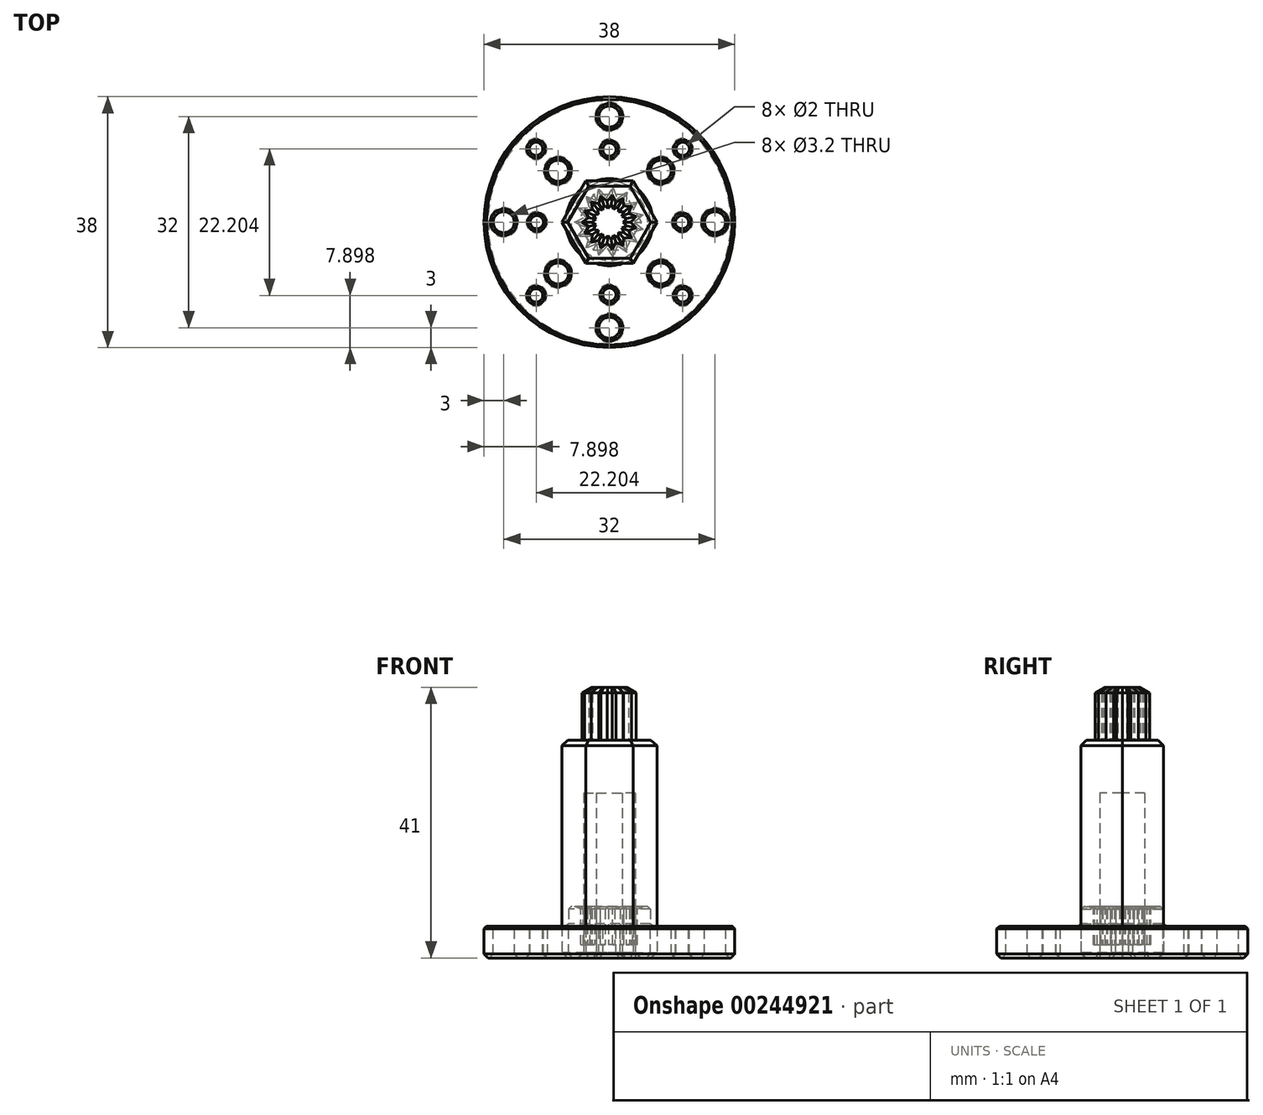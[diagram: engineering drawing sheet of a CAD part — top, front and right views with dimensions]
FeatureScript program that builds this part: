
annotation { "Feature Type Name" : "Feature", "Feature Type Description" : "" }
export const myFeature = defineFeature(function(context is Context, id is Id, definition is map)
    precondition{}
    {
        {
            var Q0;
            Q0=qCreatedBy(makeId("Top.planeOp"),FACE);
            var sketch = newSketch(context, id + "F0", { "sketchPlane" : qUnion([Q0])});
            skCircle(sketch, "E0", {"center": v(0, 0) * mm, "radius": 19 * mm});
            skSolve(sketch);
        }
        {
            var Q0;
            Q0=qSketchRegion(id+"F0",true);
            extrude(context, id + "F1", {"entities" : qUnion([Q0]), "depth" : 4.8 * mm, "offsetDistance" : 25 * mm});
        }
        {
            var Q0;
            Q0=makeQuery(id+"F1.opExtrude","CAP_FACE",FACE,{"disambiguationData":[OSD([sQuery(id+"F0.wireOp",EDGE,"ZvkXPhkh-jxfF-Gfea-dxrh-XISQfD8u4X7v"),sQuery(id+"F0.wireOp",EDGE,"E0")])],"isStart":false});
            var sketch = newSketch(context, id + "F2", { "sketchPlane" : qUnion([Q0])});
            skCircle(sketch, "E1", {"center": v(11, 0) * mm, "radius": 1 * mm});
            skCircle(sketch, "E2.1.0", {"center": v(0, 11) * mm, "radius": 1 * mm});
            skCircle(sketch, "E2.2.0", {"center": v(-11, 0) * mm, "radius": 1 * mm});
            skCircle(sketch, "E2.3.0", {"center": v(0, -11) * mm, "radius": 1 * mm});
            skPoint(sketch, "E2.center", {"position": v(0, 0) * mm});
            skCircle(sketch, "E3", {"center": v(16, 0) * mm, "radius": 1.6 * mm});
            skCircle(sketch, "E4.1.0", {"center": v(0, 16) * mm, "radius": 1.6 * mm});
            skCircle(sketch, "E4.2.0", {"center": v(-16, 0) * mm, "radius": 1.6 * mm});
            skCircle(sketch, "E4.3.0", {"center": v(0, -16) * mm, "radius": 1.6 * mm});
            skLineSegment(sketch, "E5", {"start": v(0, 0) * mm, "end": v(7.78, 7.78) * mm});
            skLineSegment(sketch, "E6", {"start": v(7.78, 7.78) * mm, "end": v(11.1, 11.1) * mm});
            skCircle(sketch, "E7", {"center": v(7.78, 7.78) * mm, "radius": 1.6 * mm});
            skCircle(sketch, "E8", {"center": v(11.1, 11.1) * mm, "radius": 1 * mm});
            skCircle(sketch, "E9.1.0", {"center": v(-7.78, 7.78) * mm, "radius": 1.6 * mm});
            skCircle(sketch, "E9.1.1", {"center": v(-11.1, 11.1) * mm, "radius": 1 * mm});
            skCircle(sketch, "E9.2.0", {"center": v(-7.78, -7.78) * mm, "radius": 1.6 * mm});
            skCircle(sketch, "E9.2.1", {"center": v(-11.1, -11.1) * mm, "radius": 1 * mm});
            skCircle(sketch, "E9.3.0", {"center": v(7.78, -7.78) * mm, "radius": 1.6 * mm});
            skCircle(sketch, "E9.3.1", {"center": v(11.1, -11.1) * mm, "radius": 1 * mm});
            skSolve(sketch);
        }
        {
            var Q0;
            Q0=qSketchRegion(id+"F2",true);
            extrude(context, id + "F3", {"entities" : qUnion([Q0]), "operationType" : NewBodyOperationType.REMOVE, "oppositeDirection" : true, "depth" : 10 * mm, "offsetDistance" : 25 * mm});
        }
        {
            var Q0;
            Q0=makeQuery(id+"F1.opExtrude","CAP_FACE",FACE,{"disambiguationData":[OSD([sQuery(id+"F0.wireOp",EDGE,"E0")])],"isStart":false});
            var sketch = newSketch(context, id + "F4", { "sketchPlane" : qUnion([Q0])});
            skCircle(sketch, "E10", {"center": v(0, 0) * mm, "radius": 6.2 * mm});
            skSolve(sketch);
        }
        {
            var Q0;
            Q0=qSketchRegion(id+"F4",true);
            extrude(context, id + "F5", {"entities" : qUnion([Q0]), "operationType" : NewBodyOperationType.ADD, "depth" : 3 * mm, "offsetDistance" : 25 * mm});
        }
        {
            var Q0;
            Q0=makeQuery(id+"F5.opExtrude","CAP_FACE",FACE,{"disambiguationData":[OSD([sQuery(id+"F4.wireOp",EDGE,"E10")])],"isStart":false});
            var sketch = newSketch(context, id + "F6", { "sketchPlane" : qUnion([Q0])});
            skLineSegment(sketch, "E11", {"start": v(3.1, 0) * mm, "end": v(4.3, 0.94) * mm});
            skLineSegment(sketch, "E12.MirrorCS", {"start": v(3.1, 0) * mm, "end": v(4.3, -0.94) * mm});
            skLineSegment(sketch, "E13.1.0", {"start": v(2.83, 1.26) * mm, "end": v(3.55, 2.6) * mm});
            skLineSegment(sketch, "E13.1.1", {"start": v(2.83, 1.26) * mm, "end": v(4.3, 0.9) * mm});
            skLineSegment(sketch, "E13.2.0", {"start": v(2.07, 2.3) * mm, "end": v(2.18, 3.82) * mm});
            skLineSegment(sketch, "E13.2.1", {"start": v(2.07, 2.3) * mm, "end": v(3.57, 2.57) * mm});
            skLineSegment(sketch, "E13.3.0", {"start": v(0.96, 2.95) * mm, "end": v(0.44, 4.38) * mm});
            skLineSegment(sketch, "E13.3.1", {"start": v(0.96, 2.95) * mm, "end": v(2.22, 3.8) * mm});
            skLineSegment(sketch, "E13.4.0", {"start": v(-0.32, 3.08) * mm, "end": v(-1.38, 4.18) * mm});
            skLineSegment(sketch, "E13.4.1", {"start": v(-0.32, 3.08) * mm, "end": v(0.48, 4.37) * mm});
            skLineSegment(sketch, "E13.5.0", {"start": v(-1.55, 2.68) * mm, "end": v(-2.96, 3.26) * mm});
            skLineSegment(sketch, "E13.5.1", {"start": v(-1.55, 2.68) * mm, "end": v(-1.34, 4.2) * mm});
            skLineSegment(sketch, "E13.6.0", {"start": v(-2.5, 1.82) * mm, "end": v(-4.03, 1.77) * mm});
            skLineSegment(sketch, "E13.6.1", {"start": v(-2.5, 1.82) * mm, "end": v(-2.93, 3.29) * mm});
            skLineSegment(sketch, "E13.7.0", {"start": v(-3.03, 0.64) * mm, "end": v(-4.4, -0.02) * mm});
            skLineSegment(sketch, "E13.7.1", {"start": v(-3.03, 0.64) * mm, "end": v(-4.01, 1.81) * mm});
            skLineSegment(sketch, "E13.8.0", {"start": v(-3.03, -0.64) * mm, "end": v(-4.01, -1.81) * mm});
            skLineSegment(sketch, "E13.8.1", {"start": v(-3.03, -0.64) * mm, "end": v(-4.4, 0.02) * mm});
            skLineSegment(sketch, "E13.9.0", {"start": v(-2.5, -1.82) * mm, "end": v(-2.93, -3.29) * mm});
            skLineSegment(sketch, "E13.9.1", {"start": v(-2.5, -1.82) * mm, "end": v(-4.03, -1.77) * mm});
            skLineSegment(sketch, "E13.10.0", {"start": v(-1.55, -2.68) * mm, "end": v(-1.34, -4.2) * mm});
            skLineSegment(sketch, "E13.10.1", {"start": v(-1.55, -2.68) * mm, "end": v(-2.96, -3.26) * mm});
            skLineSegment(sketch, "E13.11.0", {"start": v(-0.32, -3.08) * mm, "end": v(0.48, -4.37) * mm});
            skLineSegment(sketch, "E13.11.1", {"start": v(-0.32, -3.08) * mm, "end": v(-1.38, -4.18) * mm});
            skLineSegment(sketch, "E13.12.0", {"start": v(0.96, -2.95) * mm, "end": v(2.22, -3.8) * mm});
            skLineSegment(sketch, "E13.12.1", {"start": v(0.96, -2.95) * mm, "end": v(0.44, -4.38) * mm});
            skLineSegment(sketch, "E13.13.0", {"start": v(2.07, -2.3) * mm, "end": v(3.57, -2.57) * mm});
            skLineSegment(sketch, "E13.13.1", {"start": v(2.07, -2.3) * mm, "end": v(2.18, -3.82) * mm});
            skLineSegment(sketch, "E13.14.0", {"start": v(2.83, -1.26) * mm, "end": v(4.3, -0.9) * mm});
            skLineSegment(sketch, "E13.14.1", {"start": v(2.83, -1.26) * mm, "end": v(3.55, -2.6) * mm});
            skPoint(sketch, "E13.center", {"position": v(0, 0) * mm});
            skSolve(sketch);
        }
        {
            var Q0;
            Q0=qSketchRegion(id+"F6",true);
            extrude(context, id + "F7", {"entities" : qUnion([Q0]), "operationType" : NewBodyOperationType.REMOVE, "oppositeDirection" : true, "depth" : 25 * mm, "offsetDistance" : 25 * mm});
        }
        {
            var Q0;
            Q0=qCreatedBy(makeId("Top.planeOp"),FACE);
            var sketch = newSketch(context, id + "F8", { "sketchPlane" : qUnion([Q0])});
            skCircle(sketch, "E14", {"center": v(0, 0) * mm, "radius": 6 * mm});
            skCircle(sketch, "E15", {"center": v(0, 0) * mm, "radius": 1.8 * mm});
            skSolve(sketch);
        }
        {
            var Q0;
            Q0 = qSketchRegion(id + "F8", true);
            extrude(context, id + "F9", {"entities" : qUnion([Q0]), "operationType" : NewBodyOperationType.ADD, "depth" : 2 * mm, "offsetDistance" : 25 * mm});
        }
        {
            var Q0;
            Q0=makeQuery(id+"F1.opExtrude","CAP_FACE",FACE,{"disambiguationData":[OSD([sQuery(id+"F0.wireOp",EDGE,"E0")])],"isStart":true});
            chamfer(context, id + "F10", {"entities" : qUnion([Q0]), "width" : .6 * mm, "tangentPropagation" : true});
        }
        {
            var Q0;
            Q0=makeQuery(id+"F5.opExtrude","CAP_FACE",FACE,{"disambiguationData":[OSD([sQuery(id+"F4.wireOp",EDGE,"E10")])],"isStart":false});
            var Q1;
            Q1=makeQuery(id+"F1.opExtrude","CAP_FACE",FACE,{"disambiguationData":[OSD([sQuery(id+"F0.wireOp",EDGE,"E0")])],"isStart":false});
            chamfer(context, id + "F11", {"entities" : qUnion([Q0, Q1]), "width" : .4 * mm, "tangentPropagation" : true});
        }
        {
            var Q0;
            Q0=qCreatedBy(makeId("Top.planeOp"),FACE);
            var sketch = newSketch(context, id + "F12", { "sketchPlane" : qUnion([Q0])});
            skCircle(sketch, "E16.cCircle", {"center": v(0, 0) * mm, "radius": 6.25 * mm, "construction": true});
            skLineSegment(sketch, "E16.0", {"start": v(-3.6, 6.25) * mm, "end": v(3.6, 6.25) * mm});
            skLineSegment(sketch, "E16.1", {"start": v(3.6, 6.25) * mm, "end": v(7.22, 0) * mm});
            skLineSegment(sketch, "E16.2", {"start": v(7.22, 0) * mm, "end": v(3.6, -6.25) * mm});
            skLineSegment(sketch, "E16.3", {"start": v(3.6, -6.25) * mm, "end": v(-3.6, -6.25) * mm});
            skLineSegment(sketch, "E16.4", {"start": v(-3.6, -6.25) * mm, "end": v(-7.22, 0) * mm});
            skLineSegment(sketch, "E16.5", {"start": v(-7.22, 0) * mm, "end": v(-3.6, 6.25) * mm});
            skPoint(sketch, "E16.0.midPoint", {"position": v(0, 6.25) * mm});
            skSolve(sketch);
        }
        {
            var Q0;
            Q0 = qSketchRegion(id + "F12", true);
            extrude(context, id + "F13", {"entities" : qUnion([Q0]), "depth" : 30 * mm, "offsetDistance" : 25 * mm});
        }
        {
            var Q0;
            Q0=makeQuery(id+"F13.opExtrude","CAP_FACE",FACE,{"disambiguationData":[OSD([sQuery(id+"F12.wireOp",EDGE,"E16.0"),sQuery(id+"F12.wireOp",EDGE,"E16.1"),sQuery(id+"F12.wireOp",EDGE,"E16.2"),sQuery(id+"F12.wireOp",EDGE,"E16.3"),sQuery(id+"F12.wireOp",EDGE,"E16.4"),sQuery(id+"F12.wireOp",EDGE,"E16.5")])],"isStart":true});
            var sketch = newSketch(context, id + "F14", { "sketchPlane" : qUnion([Q0])});
            skCircle(sketch, "E17.cCircle", {"center": v(0, 0) * mm, "radius": 3.4 * mm, "construction": true});
            skLineSegment(sketch, "E17.0", {"start": v(-1.96, 3.4) * mm, "end": v(1.96, 3.4) * mm});
            skLineSegment(sketch, "E17.1", {"start": v(1.96, 3.4) * mm, "end": v(3.93, 0) * mm});
            skLineSegment(sketch, "E17.2", {"start": v(3.93, 0) * mm, "end": v(1.96, -3.4) * mm});
            skLineSegment(sketch, "E17.3", {"start": v(1.96, -3.4) * mm, "end": v(-1.96, -3.4) * mm});
            skLineSegment(sketch, "E17.4", {"start": v(-1.96, -3.4) * mm, "end": v(-3.93, 0) * mm});
            skLineSegment(sketch, "E17.5", {"start": v(-3.93, 0) * mm, "end": v(-1.96, 3.4) * mm});
            skPoint(sketch, "E17.0.midPoint", {"position": v(0, 3.4) * mm});
            skSolve(sketch);
        }
        {
            var Q0;
            Q0 = qSketchRegion(id + "F14", true);
            extrude(context, id + "F15", {"entities" : qUnion([Q0]), "operationType" : NewBodyOperationType.REMOVE, "oppositeDirection" : true, "depth" : 25 * mm, "offsetDistance" : 25 * mm});
        }
        {
            var Q0;
            Q0=makeQuery(id+"F13.opExtrude","CAP_FACE",FACE,{"disambiguationData":[OSD([sQuery(id+"F12.wireOp",EDGE,"E16.0"),sQuery(id+"F12.wireOp",EDGE,"E16.1"),sQuery(id+"F12.wireOp",EDGE,"E16.2"),sQuery(id+"F12.wireOp",EDGE,"E16.3"),sQuery(id+"F12.wireOp",EDGE,"E16.4"),sQuery(id+"F12.wireOp",EDGE,"E16.5")])],"isStart":false});
            var sketch = newSketch(context, id + "F16", { "sketchPlane" : qUnion([Q0])});
            skCircle(sketch, "E18.cCircle", {"center": v(0, 0) * mm, "radius": 6.25 * mm, "construction": true});
            skLineSegment(sketch, "E18.0", {"start": v(-3.6, 6.25) * mm, "end": v(3.6, 6.25) * mm});
            skLineSegment(sketch, "E18.1", {"start": v(3.6, 6.25) * mm, "end": v(7.22, 0) * mm});
            skLineSegment(sketch, "E18.2", {"start": v(7.22, 0) * mm, "end": v(3.6, -6.25) * mm});
            skLineSegment(sketch, "E18.3", {"start": v(3.6, -6.25) * mm, "end": v(-3.6, -6.25) * mm});
            skLineSegment(sketch, "E18.4", {"start": v(-3.6, -6.25) * mm, "end": v(-7.22, 0) * mm});
            skLineSegment(sketch, "E18.5", {"start": v(-7.22, 0) * mm, "end": v(-3.6, 6.25) * mm});
            skPoint(sketch, "E18.0.midPoint", {"position": v(0, 6.25) * mm});
            skSolve(sketch);
        }
        {
            var Q0;
            Q0 = qSketchRegion(id + "F16", true);
            extrude(context, id + "F17", {"entities" : qUnion([Q0]), "operationType" : NewBodyOperationType.ADD, "depth" : 3 * mm, "offsetDistance" : 25 * mm});
        }
        {
            var Q0;
            Q0=makeQuery(id+"F17.opExtrude","CAP_FACE",FACE,{"disambiguationData":[OSD([sQuery(id+"F16.wireOp",EDGE,"E18.0"),sQuery(id+"F16.wireOp",EDGE,"E18.1"),sQuery(id+"F16.wireOp",EDGE,"E18.2"),sQuery(id+"F16.wireOp",EDGE,"E18.3"),sQuery(id+"F16.wireOp",EDGE,"E18.4"),sQuery(id+"F16.wireOp",EDGE,"E18.5")])],"isStart":false});
            var Q1;
            Q1=makeQuery(id+"F13.opExtrude","CAP_FACE",FACE,{"disambiguationData":[OSD([sQuery(id+"F12.wireOp",EDGE,"E16.0"),sQuery(id+"F12.wireOp",EDGE,"E16.1"),sQuery(id+"F12.wireOp",EDGE,"E16.2"),sQuery(id+"F12.wireOp",EDGE,"E16.3"),sQuery(id+"F12.wireOp",EDGE,"E16.4"),sQuery(id+"F12.wireOp",EDGE,"E16.5")])],"isStart":true});
            chamfer(context, id + "F18", {"entities" : qUnion([Q0, Q1]), "width" : .8 * mm, "tangentPropagation" : true});
        }
        {
            var Q0;
            Q0=makeQuery(id+"F17.opExtrude","CAP_FACE",FACE,{"disambiguationData":[OSD([sQuery(id+"F16.wireOp",EDGE,"E18.0"),sQuery(id+"F16.wireOp",EDGE,"E18.1"),sQuery(id+"F16.wireOp",EDGE,"E18.2"),sQuery(id+"F16.wireOp",EDGE,"E18.3"),sQuery(id+"F16.wireOp",EDGE,"E18.4"),sQuery(id+"F16.wireOp",EDGE,"E18.5")])],"isStart":false});
            var sketch = newSketch(context, id + "F19", { "sketchPlane" : qUnion([Q0])});
            skLineSegment(sketch, "E19", {"start": v(3.2, 0) * mm, "end": v(4.1, 0.9) * mm});
            skLineSegment(sketch, "E20.MirrorCS", {"start": v(3.2, 0) * mm, "end": v(4.1, -0.9) * mm});
            skLineSegment(sketch, "E21.1.0", {"start": v(2.92, 1.3) * mm, "end": v(4.11, 0.85) * mm});
            skLineSegment(sketch, "E21.1.1", {"start": v(2.92, 1.3) * mm, "end": v(3.38, 2.49) * mm});
            skLineSegment(sketch, "E21.2.0", {"start": v(2.14, 2.38) * mm, "end": v(3.41, 2.44) * mm});
            skLineSegment(sketch, "E21.2.1", {"start": v(2.14, 2.38) * mm, "end": v(2.07, 3.65) * mm});
            skLineSegment(sketch, "E21.3.0", {"start": v(0.99, 3.04) * mm, "end": v(2.12, 3.62) * mm});
            skLineSegment(sketch, "E21.3.1", {"start": v(0.99, 3.04) * mm, "end": v(0.41, 4.18) * mm});
            skLineSegment(sketch, "E21.4.0", {"start": v(-0.33, 3.18) * mm, "end": v(0.47, 4.17) * mm});
            skLineSegment(sketch, "E21.4.1", {"start": v(-0.33, 3.18) * mm, "end": v(-1.32, 3.98) * mm});
            skLineSegment(sketch, "E21.5.0", {"start": v(-1.6, 2.77) * mm, "end": v(-1.27, 4) * mm});
            skLineSegment(sketch, "E21.5.1", {"start": v(-1.6, 2.77) * mm, "end": v(-2.83, 3.1) * mm});
            skLineSegment(sketch, "E21.6.0", {"start": v(-2.59, 1.88) * mm, "end": v(-2.79, 3.14) * mm});
            skLineSegment(sketch, "E21.6.1", {"start": v(-2.59, 1.88) * mm, "end": v(-3.85, 1.68) * mm});
            skLineSegment(sketch, "E21.7.0", {"start": v(-3.13, 0.67) * mm, "end": v(-3.82, 1.73) * mm});
            skLineSegment(sketch, "E21.7.1", {"start": v(-3.13, 0.67) * mm, "end": v(-4.2, -0.03) * mm});
            skLineSegment(sketch, "E21.8.0", {"start": v(-3.13, -0.67) * mm, "end": v(-4.2, 0.03) * mm});
            skLineSegment(sketch, "E21.8.1", {"start": v(-3.13, -0.67) * mm, "end": v(-3.82, -1.73) * mm});
            skLineSegment(sketch, "E21.9.0", {"start": v(-2.59, -1.88) * mm, "end": v(-3.85, -1.68) * mm});
            skLineSegment(sketch, "E21.9.1", {"start": v(-2.59, -1.88) * mm, "end": v(-2.79, -3.14) * mm});
            skLineSegment(sketch, "E21.10.0", {"start": v(-1.6, -2.77) * mm, "end": v(-2.83, -3.1) * mm});
            skLineSegment(sketch, "E21.10.1", {"start": v(-1.6, -2.77) * mm, "end": v(-1.27, -4) * mm});
            skLineSegment(sketch, "E21.11.0", {"start": v(-0.33, -3.18) * mm, "end": v(-1.32, -3.98) * mm});
            skLineSegment(sketch, "E21.11.1", {"start": v(-0.33, -3.18) * mm, "end": v(0.47, -4.17) * mm});
            skLineSegment(sketch, "E21.12.0", {"start": v(0.99, -3.04) * mm, "end": v(0.41, -4.18) * mm});
            skLineSegment(sketch, "E21.12.1", {"start": v(0.99, -3.04) * mm, "end": v(2.12, -3.62) * mm});
            skLineSegment(sketch, "E21.13.0", {"start": v(2.14, -2.38) * mm, "end": v(2.07, -3.65) * mm});
            skLineSegment(sketch, "E21.13.1", {"start": v(2.14, -2.38) * mm, "end": v(3.41, -2.44) * mm});
            skLineSegment(sketch, "E21.14.0", {"start": v(2.92, -1.3) * mm, "end": v(3.38, -2.49) * mm});
            skLineSegment(sketch, "E21.14.1", {"start": v(2.92, -1.3) * mm, "end": v(4.11, -0.85) * mm});
            skPoint(sketch, "E21.center", {"position": v(0, 0) * mm});
            skSolve(sketch);
        }
        {
            var Q0;
            Q0 = qSketchRegion(id + "F19", true);
            extrude(context, id + "F20", {"entities" : qUnion([Q0]), "operationType" : NewBodyOperationType.ADD, "depth" : 8 * mm, "offsetDistance" : 25 * mm});
        }
        {
            var Q0;
            Q0=makeQuery(id+"F13.opExtrude","CAP_FACE",FACE,{"disambiguationData":[OSD([sQuery(id+"F12.wireOp",EDGE,"N6ndEIrb-N8uo-6AdX-TBZU-aG1VvkIupD5g")])],"isStart":true});
            var Q1;
            Q1=makeQuery(id+"F20.opExtrude","CAP_FACE",FACE,{"disambiguationData":[OSD([sQuery(id+"F19.wireOp",EDGE,"E19"),sQuery(id+"F19.wireOp",EDGE,"E20.MirrorCS"),sQuery(id+"F19.wireOp",EDGE,"E21.1.0"),sQuery(id+"F19.wireOp",EDGE,"E21.1.1"),sQuery(id+"F19.wireOp",EDGE,"E21.2.0"),sQuery(id+"F19.wireOp",EDGE,"E21.2.1"),sQuery(id+"F19.wireOp",EDGE,"E21.3.0"),sQuery(id+"F19.wireOp",EDGE,"E21.3.1"),sQuery(id+"F19.wireOp",EDGE,"E21.4.0"),sQuery(id+"F19.wireOp",EDGE,"E21.4.1"),sQuery(id+"F19.wireOp",EDGE,"E21.5.0"),sQuery(id+"F19.wireOp",EDGE,"E21.5.1"),sQuery(id+"F19.wireOp",EDGE,"E21.6.0"),sQuery(id+"F19.wireOp",EDGE,"E21.6.1"),sQuery(id+"F19.wireOp",EDGE,"E21.7.0"),sQuery(id+"F19.wireOp",EDGE,"E21.7.1"),sQuery(id+"F19.wireOp",EDGE,"E21.8.0"),sQuery(id+"F19.wireOp",EDGE,"E21.8.1"),sQuery(id+"F19.wireOp",EDGE,"E21.9.0"),sQuery(id+"F19.wireOp",EDGE,"E21.9.1"),sQuery(id+"F19.wireOp",EDGE,"E21.10.0"),sQuery(id+"F19.wireOp",EDGE,"E21.10.1"),sQuery(id+"F19.wireOp",EDGE,"E21.11.0"),sQuery(id+"F19.wireOp",EDGE,"E21.11.1"),sQuery(id+"F19.wireOp",EDGE,"E21.12.0"),sQuery(id+"F19.wireOp",EDGE,"E21.12.1"),sQuery(id+"F19.wireOp",EDGE,"E21.13.0"),sQuery(id+"F19.wireOp",EDGE,"E21.13.1"),sQuery(id+"F19.wireOp",EDGE,"E21.14.0"),sQuery(id+"F19.wireOp",EDGE,"E21.14.1")])],"isStart":false});
            chamfer(context, id + "F21", {"entities" : qUnion([Q0, Q1]), "width" : .8 * mm, "tangentPropagation" : true});
        }
    });
